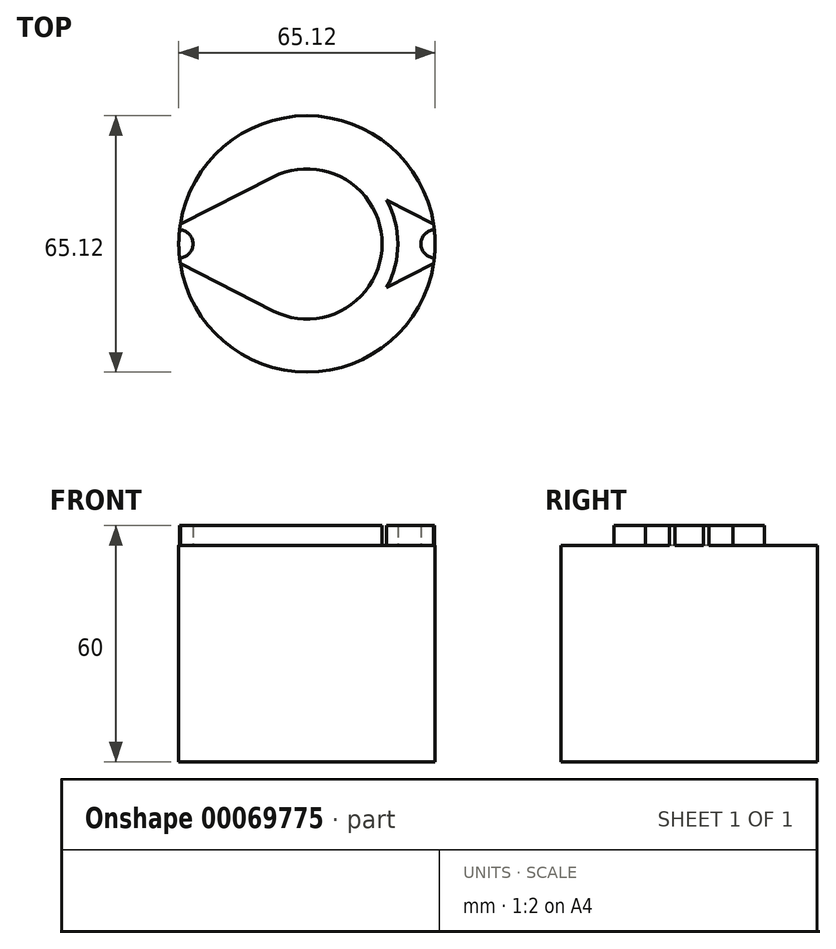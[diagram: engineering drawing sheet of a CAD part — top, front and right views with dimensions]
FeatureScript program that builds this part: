
annotation { "Feature Type Name" : "Feature", "Feature Type Description" : "" }
export const myFeature = defineFeature(function(context is Context, id is Id, definition is map)
    precondition{}
    {
        {
            var Q0;
            Q0=qCreatedBy(makeId("Front.planeOp"),FACE);
            var sketch = newSketch(context, id + "F0", { "sketchPlane" : qUnion([Q0])});
            skLineSegment(sketch, "E0", {"start": v(0, 0) * mm, "end": v(8.6, 0) * mm});
            skLineSegment(sketch, "E1", {"start": v(0, 0) * mm, "end": v(0, -4) * mm});
            skLineSegment(sketch, "E2", {"start": v(0, -4) * mm, "end": v(6.72, -4) * mm});
            skLineSegment(sketch, "E3", {"start": v(6.72, -4) * mm, "end": v(8.63, -5.1) * mm});
            skLineSegment(sketch, "E4", {"start": v(8.63, -5.1) * mm, "end": v(11.58, -5.1) * mm});
            skLineSegment(sketch, "E5", {"start": v(0, 0) * mm, "end": v(0, 41.85) * mm, "construction": true});
            skLineSegment(sketch, "E6", {"start": v(0, 41.85) * mm, "end": v(19.09, 41.85) * mm, "construction": true});
            skLineSegment(sketch, "E7", {"start": v(19.09, 41.85) * mm, "end": v(8.6, 0) * mm, "construction": true});
            skLineSegment(sketch, "E8", {"start": v(11.58, -5.1) * mm, "end": v(23.09, 40.85) * mm, "construction": true});
            skLineSegment(sketch, "E9", {"start": v(23.09, 40.85) * mm, "end": v(19.09, 41.85) * mm, "construction": true});
            skFitSpline(sketch, "E10", {"points": [v(8.6, 0) * mm, v(13.36, 10.26) * mm, v(19.09, 41.85) * mm], "startDerivative": vector(9.96, 0) * mm, "endDerivative": vector(5.92, 58.79) * mm});
            skFitSpline(sketch, "E11", {"points": [v(11.58, -5.1) * mm, v(17.24, 9.3) * mm, v(23.09, 40.85) * mm], "startDerivative": vector(10.63, 0) * mm, "endDerivative": vector(8.03, 59.74) * mm});
            skLineSegment(sketch, "E12", {"start": v(19.09, 41.85) * mm, "end": v(23.09, 41.85) * mm});
            skLineSegment(sketch, "E13", {"start": v(23.09, 41.85) * mm, "end": v(23.09, 40.85) * mm});
            skLineSegment(sketch, "E14", {"start": v(17.24, 9.3) * mm, "end": v(13.36, 10.26) * mm, "construction": true});
            skSolve(sketch);
        }
        {
            var Q0;
            Q0=makeQuery(id+"F0.imprint","IMPRINT",FACE,{"disambiguationData":[TD([[makeQuery(id+"F0.imprint","IMPRINT",EDGE,{"derivedFrom":sQuery(id+"F0.wireOp",EDGE,"E0")}),-1.0]])]});
            var Q1;
            Q1=sQuery(id+"F0.wireOp",EDGE,"E5");
            revolve(context, id + "F1", {"entities" : qUnion([Q0]), "axis" : qUnion([Q1]), "revolveType" : RevolveType.FULL});
        }
        {
            var Q0;
            Q0=makeQuery(id+"F1.opRevolve","SWEPT_FACE",FACE,{"disambiguationData":[OSD([sQuery(id+"F0.wireOp",EDGE,"E12")])]});
            var sketch = newSketch(context, id + "F2", { "sketchPlane" : qUnion([Q0])});
            skCircle(sketch, "E15", {"center": v(0, 0) * mm, "radius": 32.56 * mm});
            skSolve(sketch);
        }
        {
            var Q0;
            Q0=makeQuery(id+"F2.imprint","IMPRINT",FACE,{"disambiguationData":[TD([[makeQuery(id+"F2.imprint","IMPRINT",EDGE,{"derivedFrom":sQuery(id+"F2.wireOp",EDGE,"E15")}),1.0]])]});
            var Q1;
            {var subQ0=sQuery(id+"F0.wireOp",EDGE,"E12");Q1=makeQuery(id+"F2.imprint","IMPRINT",FACE,{"disambiguationData":[TD([[makeQuery(id+"F2.imprint","IMPRINT",EDGE,{"derivedFrom":makeQuery(id+"F1.opRevolve","SWEPT_EDGE",EDGE,{"disambiguationData":[OSD([sQuery(id+"F0.wireOp",EDGE,"E10"),subQ0])]})}),1.0]])]});}
            var Q2;
            Q2=makeQuery(id+"F2.imprint","IMPRINT",FACE,{"disambiguationData":[TD([[makeQuery(id+"F2.imprint","IMPRINT",EDGE,{"derivedFrom":makeQuery(id+"F1.opRevolve","SWEPT_EDGE",EDGE,{"disambiguationData":[OSD([sQuery(id+"F0.wireOp",EDGE,"E10"),sQuery(id+"F0.wireOp",EDGE,"E12")])]})}),-1.0]])]});
            extrude(context, id + "F3", {"entities" : qUnion([Q0, Q1, Q2]), "oppositeDirection" : true, "depth" : 55 * mm});
        }
        {
            var Q0;
            Q0=makeQuery(id+"F1.opRevolve","SWEPT_BODY",BODY,{"disambiguationData":[OSD([sQuery(id+"F0.wireOp",EDGE,"E0"),sQuery(id+"F0.wireOp",EDGE,"E1"),sQuery(id+"F0.wireOp",EDGE,"E2"),sQuery(id+"F0.wireOp",EDGE,"E3"),sQuery(id+"F0.wireOp",EDGE,"E4"),sQuery(id+"F0.wireOp",EDGE,"E10"),sQuery(id+"F0.wireOp",EDGE,"E11"),sQuery(id+"F0.wireOp",EDGE,"E12"),sQuery(id+"F0.wireOp",EDGE,"E13")])]});
            var Q1;
            Q1=makeQuery(id+"F3.opExtrude","SWEPT_BODY",BODY,{"disambiguationData":[OSD([sQuery(id+"F2.wireOp",EDGE,"E15")])]});
            booleanBodies(context, id + "F4", {"operationType" : BooleanOperationType.SUBTRACTION, "tools" : qUnion([Q0]), "targets" : qUnion([Q1]), "keepTools" : true});
        }
        {
            var Q0;
            {var subQ0=sQuery(id+"F2.wireOp",EDGE,"E15");Q0=makeQuery(id+"F4.opBoolean","SPLIT",FACE,{"disambiguationData":[TD([makeQuery(id+"F1.opRevolve","SWEPT_FACE",FACE,{"disambiguationData":[OSD([sQuery(id+"F0.wireOp",EDGE,"E13")])]})])],"derivedFrom":makeQuery(id+"F3.opExtrude","CAP_FACE",FACE,{"disambiguationData":[OSD([subQ0])],"isStart":true})});}
            var sketch = newSketch(context, id + "F5", { "sketchPlane" : qUnion([Q0])});
            skCircle(sketch, "E16.0", {"center": v(0, 0) * mm, "radius": 32.56 * mm});
            skCircle(sketch, "E17.0", {"center": v(0, 0) * mm, "radius": 19.09 * mm});
            skLineSegment(sketch, "E18", {"start": v(-32.17, 5) * mm, "end": v(-8.68, 17) * mm});
            skLineSegment(sketch, "E19", {"start": v(0, 0) * mm, "end": v(0, 19.09) * mm, "construction": true});
            skLineSegment(sketch, "E20", {"start": v(0, 0) * mm, "end": v(-19.09, 0) * mm, "construction": true});
            skLineSegment(sketch, "E21.MirrorCS", {"start": v(32.17, 5) * mm, "end": v(8.68, 17) * mm});
            skLineSegment(sketch, "E22.MirrorCS", {"start": v(-32.17, -5) * mm, "end": v(-8.68, -17) * mm});
            skLineSegment(sketch, "E23.MirrorCS", {"start": v(32.17, -5) * mm, "end": v(8.68, -17) * mm});
            skSolve(sketch);
        }
        {
            var Q0;
            {var subQ0=sQuery(id+"F5.wireOp",EDGE,"E17.0");var subQ1=makeQuery(id+"F5.imprint","INTERSECT",VERTEX,{"derivedFrom":[subQ0,sQuery(id+"F5.wireOp",EDGE,"E18")]});Q0=makeQuery(id+"F5.imprint","IMPRINT",FACE,{"disambiguationData":[TD([[makeQuery(id+"F5.imprint","IMPRINT",EDGE,{"disambiguationData":[TD([[subQ1,-1.0]])],"derivedFrom":subQ0}),-1.0]])]});}
            var Q1;
            {var subQ0=sQuery(id+"F5.wireOp",EDGE,"E18");var subQ1=sQuery(id+"F5.wireOp",EDGE,"E17.0");var subQ2=makeQuery(id+"F5.imprint","INTERSECT",VERTEX,{"derivedFrom":[subQ1,subQ0]});Q1=makeQuery(id+"F5.imprint","IMPRINT",FACE,{"disambiguationData":[TD([[makeQuery(id+"F5.imprint","IMPRINT",EDGE,{"disambiguationData":[TD([[subQ2,1.0]])],"derivedFrom":subQ1}),1.0]])]});}
            var Q2;
            {var subQ0=sQuery(id+"F5.wireOp",EDGE,"E18");var subQ1=sQuery(id+"F5.wireOp",EDGE,"E16.0");var subQ2=makeQuery(id+"F5.imprint","INTERSECT",VERTEX,{"derivedFrom":[subQ1,subQ0]});Q2=makeQuery(id+"F5.imprint","IMPRINT",FACE,{"disambiguationData":[TD([[makeQuery(id+"F5.imprint","IMPRINT",EDGE,{"disambiguationData":[TD([[subQ2,-1.0]])],"derivedFrom":subQ1}),1.0]])]});}
            var Q3;
            {var subQ0=sQuery(id+"F5.wireOp",EDGE,"E21.MirrorCS");var subQ1=sQuery(id+"F5.wireOp",EDGE,"E17.0");var subQ2=makeQuery(id+"F5.imprint","INTERSECT",VERTEX,{"derivedFrom":[subQ1,subQ0]});Q3=makeQuery(id+"F5.imprint","IMPRINT",FACE,{"disambiguationData":[TD([[makeQuery(id+"F5.imprint","IMPRINT",EDGE,{"disambiguationData":[TD([[subQ2,-1.0]])],"derivedFrom":subQ1}),1.0]])]});}
            var Q4;
            {var subQ0=sQuery(id+"F5.wireOp",EDGE,"E21.MirrorCS");var subQ1=sQuery(id+"F5.wireOp",EDGE,"E16.0");var subQ2=makeQuery(id+"F5.imprint","INTERSECT",VERTEX,{"derivedFrom":[subQ1,subQ0]});Q4=makeQuery(id+"F5.imprint","IMPRINT",FACE,{"disambiguationData":[TD([[makeQuery(id+"F5.imprint","IMPRINT",EDGE,{"disambiguationData":[TD([[subQ2,1.0]])],"derivedFrom":subQ1}),1.0]])]});}
            extrude(context, id + "F6", {"entities" : qUnion([Q0, Q1, Q2, Q3, Q4]), "operationType" : NewBodyOperationType.ADD, "depth" : 5 * mm});
        }
        {
            var Q0;
            {var subQ0=sQuery(id+"F2.wireOp",EDGE,"E15");Q0=makeQuery(id+"F4.opBoolean","SPLIT",FACE,{"disambiguationData":[TD([makeQuery(id+"F1.opRevolve","SWEPT_FACE",FACE,{"disambiguationData":[OSD([sQuery(id+"F0.wireOp",EDGE,"E13")])]})])],"derivedFrom":makeQuery(id+"F3.opExtrude","CAP_FACE",FACE,{"disambiguationData":[OSD([subQ0])],"isStart":true})});}
            var sketch = newSketch(context, id + "F7", { "sketchPlane" : qUnion([Q0])});
            skCircle(sketch, "E24.0.0", {"center": v(0, 0) * mm, "radius": 32.56 * mm});
            skCircle(sketch, "E25", {"center": v(-32.56, 0) * mm, "radius": 3 * mm});
            skLineSegment(sketch, "E26", {"start": v(0, 0) * mm, "end": v(0, 26.65) * mm, "construction": true});
            skCircle(sketch, "E27.MirrorC", {"center": v(32.56, 0) * mm, "radius": 3 * mm});
            skSolve(sketch);
        }
        {
            var Q0;
            {var subQ0=sQuery(id+"F7.wireOp",EDGE,"E25");var subQ1=sQuery(id+"F7.wireOp",EDGE,"E24.0.0");var subQ2=makeQuery(id+"F7.imprint","INTERSECT",VERTEX,{"disambiguationData":[OD(0.0)],"derivedFrom":[subQ1,subQ0]});Q0=makeQuery(id+"F7.imprint","IMPRINT",FACE,{"disambiguationData":[TD([[makeQuery(id+"F7.imprint","IMPRINT",EDGE,{"disambiguationData":[TD([[subQ2,-1.0]])],"derivedFrom":subQ1}),1.0]])]});}
            var Q1;
            {var subQ0=sQuery(id+"F7.wireOp",EDGE,"E27.MirrorC");var subQ1=sQuery(id+"F7.wireOp",EDGE,"E24.0.0");var subQ2=makeQuery(id+"F7.imprint","INTERSECT",VERTEX,{"disambiguationData":[OD(0.0)],"derivedFrom":[subQ1,subQ0]});Q1=makeQuery(id+"F7.imprint","IMPRINT",FACE,{"disambiguationData":[TD([[makeQuery(id+"F7.imprint","IMPRINT",EDGE,{"disambiguationData":[TD([[subQ2,1.0]])],"derivedFrom":subQ1}),1.0]])]});}
            extrude(context, id + "F8", {"entities" : qUnion([Q0, Q1]), "operationType" : NewBodyOperationType.ADD, "depth" : 8 * mm});
        }
        {
            var Q0;
            {var subQ0=sQuery(id+"F2.wireOp",EDGE,"E15");Q0=makeQuery(id+"F4.opBoolean","SPLIT",FACE,{"disambiguationData":[TD([makeQuery(id+"F1.opRevolve","SWEPT_FACE",FACE,{"disambiguationData":[OSD([sQuery(id+"F0.wireOp",EDGE,"E13")])]})])],"derivedFrom":makeQuery(id+"F3.opExtrude","CAP_FACE",FACE,{"disambiguationData":[OSD([subQ0])],"isStart":true})});}
            var sketch = newSketch(context, id + "F9", { "sketchPlane" : qUnion([Q0])});
            skArc(sketch, "E28.0.0", {"start": v(-32.42, -3) * mm, "mid": v(0, -32.56) * mm, "end": v(32.42, -3) * mm});
            skArc(sketch, "E28.0.1", {"start": v(32.42, -3) * mm, "mid": v(29.56, 0) * mm, "end": v(32.42, 3) * mm});
            skArc(sketch, "E28.0.2", {"start": v(32.42, 3) * mm, "mid": v(0, 32.56) * mm, "end": v(-32.42, 3) * mm});
            skArc(sketch, "E28.0.3", {"start": v(-32.42, 3) * mm, "mid": v(-29.56, 0) * mm, "end": v(-32.42, -3) * mm});
            skCircle(sketch, "E29", {"center": v(-32.56, 0) * mm, "radius": 3.6 * mm});
            skCircle(sketch, "E30", {"center": v(32.56, 0) * mm, "radius": 3.6 * mm});
            skSolve(sketch);
        }
        {
            var Q0;
            {var subQ0=sQuery(id+"F9.wireOp",EDGE,"E28.0.3");Q0=makeQuery(id+"F9.imprint","IMPRINT",FACE,{"disambiguationData":[TD([[makeQuery(id+"F9.imprint","IMPRINT",EDGE,{"derivedFrom":subQ0}),-1.0]])]});}
            var Q1;
            {var subQ0=sQuery(id+"F9.wireOp",EDGE,"E28.0.3");Q1=makeQuery(id+"F9.imprint","IMPRINT",FACE,{"disambiguationData":[TD([[makeQuery(id+"F9.imprint","IMPRINT",EDGE,{"derivedFrom":subQ0}),1.0]])]});}
            var Q2;
            {var subQ0=sQuery(id+"F9.wireOp",EDGE,"E28.0.1");Q2=makeQuery(id+"F9.imprint","IMPRINT",FACE,{"disambiguationData":[TD([[makeQuery(id+"F9.imprint","IMPRINT",EDGE,{"derivedFrom":subQ0}),1.0]])]});}
            var Q3;
            {var subQ0=sQuery(id+"F9.wireOp",EDGE,"E28.0.1");Q3=makeQuery(id+"F9.imprint","IMPRINT",FACE,{"disambiguationData":[TD([[makeQuery(id+"F9.imprint","IMPRINT",EDGE,{"derivedFrom":subQ0}),-1.0]])]});}
            extrude(context, id + "F10", {"entities" : qUnion([Q0, Q1, Q2, Q3]), "operationType" : NewBodyOperationType.REMOVE, "depth" : 25 * mm});
        }
    });
